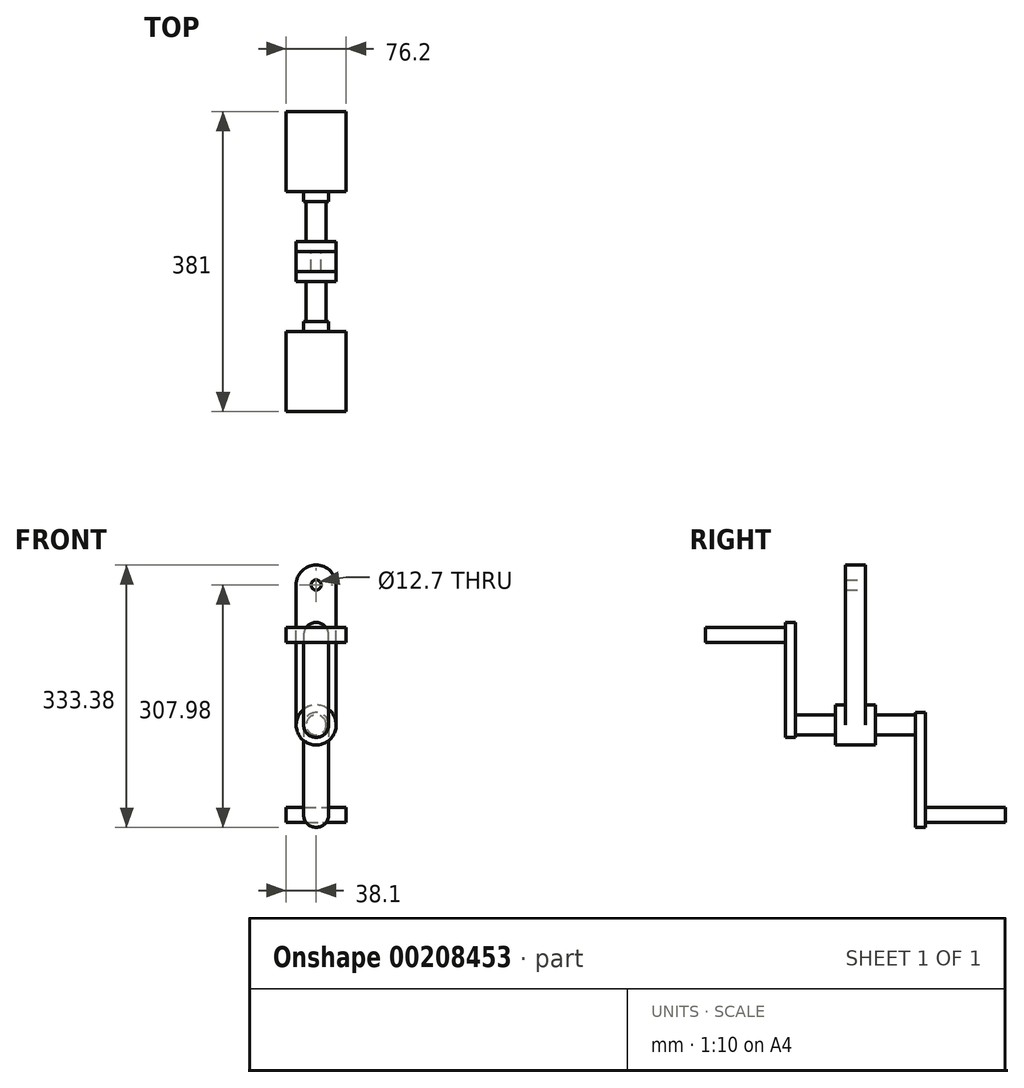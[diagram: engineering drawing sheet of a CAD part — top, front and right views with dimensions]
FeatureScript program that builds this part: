
annotation { "Feature Type Name" : "Feature", "Feature Type Description" : "" }
export const myFeature = defineFeature(function(context is Context, id is Id, definition is map)
    precondition{}
    {
        {
            var Q0;
            Q0=qCreatedBy(makeId("Front.planeOp"),FACE);
            var sketch = newSketch(context, id + "F0", { "sketchPlane" : qUnion([Q0])});
            skCircle(sketch, "E0", {"center": v(0, 0) * mm, "radius": 25.4 * mm});
            skCircle(sketch, "E1", {"center": v(0, 0) * mm, "radius": 12.7 * mm});
            skSolve(sketch);
        }
        {
            var Q0;
            Q0=qSketchRegion(id+"F0",true);
            extrude(context, id + "F1", {"entities" : qUnion([Q0]), "endBound" : BoundingType.SYMMETRIC, "depth" : 50.8 * mm});
        }
        {
            var Q0;
            Q0=qCreatedBy(makeId("Front.planeOp"),FACE);
            var sketch = newSketch(context, id + "F2", { "sketchPlane" : qUnion([Q0])});
            skCircle(sketch, "E2", {"center": v(0, 0) * mm, "radius": 12.7 * mm});
            skSolve(sketch);
        }
        {
            var Q0;
            Q0=qSketchRegion(id+"F2",true);
            extrude(context, id + "F3", {"entities" : qUnion([Q0]), "endBound" : BoundingType.SYMMETRIC, "depth" : 152.4 * mm});
        }
        {
            var Q0;
            Q0=makeQuery(id+"F3.opExtrude","CAP_FACE",FACE,{"disambiguationData":[OSD([sQuery(id+"F2.wireOp",EDGE,"E2")])],"isStart":false});
            var sketch = newSketch(context, id + "F4", { "sketchPlane" : qUnion([Q0])});
            skArc(sketch, "E3", {"start": v(-15.88, 0) * mm, "mid": v(0, -15.88) * mm, "end": v(15.88, 0) * mm});
            skArc(sketch, "E4", {"start": v(15.87, 114.3) * mm, "mid": v(0, 130.18) * mm, "end": v(-15.88, 114.3) * mm});
            skLineSegment(sketch, "E5", {"start": v(-15.88, 114.3) * mm, "end": v(-15.88, 0) * mm});
            skLineSegment(sketch, "E6", {"start": v(15.88, 0) * mm, "end": v(15.88, 114.3) * mm});
            skSolve(sketch);
        }
        {
            var Q0;
            Q0=qSketchRegion(id+"F4",true);
            extrude(context, id + "F5", {"entities" : qUnion([Q0]), "operationType" : NewBodyOperationType.ADD, "depth" : 12.7 * mm});
        }
        {
            var Q0;
            Q0=makeQuery(id+"F5.opExtrude","CAP_FACE",FACE,{"disambiguationData":[OSD([sQuery(id+"F4.wireOp",EDGE,"E3"),sQuery(id+"F4.wireOp",EDGE,"E4"),sQuery(id+"F4.wireOp",EDGE,"E5"),sQuery(id+"F4.wireOp",EDGE,"E6")])],"isStart":false});
            var sketch = newSketch(context, id + "F6", { "sketchPlane" : qUnion([Q0])});
            skLineSegment(sketch, "E7.bottom", {"start": v(38.1, 123.83) * mm, "end": v(-38.1, 123.83) * mm});
            skLineSegment(sketch, "E7.top", {"start": v(38.1, 104.78) * mm, "end": v(-38.1, 104.78) * mm});
            skLineSegment(sketch, "E7.left", {"start": v(38.1, 123.83) * mm, "end": v(38.1, 104.78) * mm});
            skLineSegment(sketch, "E7.right", {"start": v(-38.1, 123.83) * mm, "end": v(-38.1, 104.78) * mm});
            skPoint(sketch, "E7.middle", {"position": v(0, 114.3) * mm});
            skPoint(sketch, "E8.orphan", {"position": v(-15.88, 114.3) * mm});
            skPoint(sketch, "E9.end.orphan", {"position": v(15.88, 114.3) * mm});
            skSolve(sketch);
        }
        {
            var Q0;
            Q0=qSketchRegion(id+"F6",true);
            extrude(context, id + "F7", {"entities" : qUnion([Q0]), "operationType" : NewBodyOperationType.ADD, "depth" : 101.6 * mm});
        }
        {
            var Q0;
            Q0=makeQuery(id+"F3.opExtrude","CAP_FACE",FACE,{"disambiguationData":[OSD([sQuery(id+"F2.wireOp",EDGE,"E2")])],"isStart":true});
            var sketch = newSketch(context, id + "F8", { "sketchPlane" : qUnion([Q0])});
            skArc(sketch, "E10", {"start": v(15.88, 0) * mm, "mid": v(0, 15.88) * mm, "end": v(-15.88, 0) * mm});
            skArc(sketch, "E11", {"start": v(-15.87, -114.3) * mm, "mid": v(0, -130.18) * mm, "end": v(15.88, -114.3) * mm});
            skLineSegment(sketch, "E12", {"start": v(-15.88, 0) * mm, "end": v(-15.88, -114.3) * mm});
            skLineSegment(sketch, "E13", {"start": v(15.88, 0) * mm, "end": v(15.88, -114.3) * mm});
            skSolve(sketch);
        }
        {
            var Q0;
            Q0=qSketchRegion(id+"F8",true);
            extrude(context, id + "F9", {"entities" : qUnion([Q0]), "operationType" : NewBodyOperationType.ADD, "depth" : 12.7 * mm});
        }
        {
            var Q0;
            Q0=makeQuery(id+"F9.opExtrude","CAP_FACE",FACE,{"disambiguationData":[OSD([sQuery(id+"F8.wireOp",EDGE,"E10"),sQuery(id+"F8.wireOp",EDGE,"E11"),sQuery(id+"F8.wireOp",EDGE,"E12"),sQuery(id+"F8.wireOp",EDGE,"E13")])],"isStart":false});
            var sketch = newSketch(context, id + "F10", { "sketchPlane" : qUnion([Q0])});
            skLineSegment(sketch, "E14.bottom", {"start": v(38.1, -104.78) * mm, "end": v(-38.1, -104.78) * mm});
            skLineSegment(sketch, "E14.top", {"start": v(38.1, -123.83) * mm, "end": v(-38.1, -123.83) * mm});
            skLineSegment(sketch, "E14.left", {"start": v(38.1, -104.78) * mm, "end": v(38.1, -123.83) * mm});
            skLineSegment(sketch, "E14.right", {"start": v(-38.1, -104.78) * mm, "end": v(-38.1, -123.83) * mm});
            skPoint(sketch, "E14.middle", {"position": v(0, -114.3) * mm});
            skPoint(sketch, "E15.orphan", {"position": v(-15.88, -114.3) * mm});
            skPoint(sketch, "E16.start.orphan", {"position": v(15.88, -114.3) * mm});
            skSolve(sketch);
        }
        {
            var Q0;
            Q0=qSketchRegion(id+"F10",true);
            extrude(context, id + "F11", {"entities" : qUnion([Q0]), "operationType" : NewBodyOperationType.ADD, "depth" : 101.6 * mm});
        }
        {
            var Q0;
            Q0=qCreatedBy(makeId("Front.planeOp"),FACE);
            var sketch = newSketch(context, id + "F12", { "sketchPlane" : qUnion([Q0])});
            skLineSegment(sketch, "E17.bottom", {"start": v(-25.4, 0) * mm, "end": v(25.4, 0) * mm});
            skLineSegment(sketch, "E17.top", {"start": v(0, 203.2) * mm, "end": v(0, 203.2) * mm});
            skLineSegment(sketch, "E17.left", {"start": v(-25.4, 0) * mm, "end": v(-25.4, 177.8) * mm});
            skLineSegment(sketch, "E17.right", {"start": v(25.4, 0) * mm, "end": v(25.4, 177.8) * mm});
            skPoint(sketch, "E18.visualSharp", {"position": v(-25.4, 203.2) * mm});
            skArc(sketch, "E18.filletArc", {"start": v(0, 203.2) * mm, "mid": v(-17.96, 195.76) * mm, "end": v(-25.4, 177.8) * mm});
            skPoint(sketch, "E19.visualSharp", {"position": v(25.4, 203.2) * mm});
            skArc(sketch, "E19.filletArc", {"start": v(25.4, 177.8) * mm, "mid": v(17.96, 195.76) * mm, "end": v(0, 203.2) * mm});
            skLineSegment(sketch, "E20", {"start": v(0, 0) * mm, "end": v(25.4, 0) * mm});
            skCircle(sketch, "E21", {"center": v(0, 177.8) * mm, "radius": 6.35 * mm});
            skSolve(sketch);
        }
        {
            var Q0;
            Q0=qSketchRegion(id+"F12",true);
            extrude(context, id + "F13", {"entities" : qUnion([Q0]), "operationType" : NewBodyOperationType.ADD, "endBound" : BoundingType.SYMMETRIC, "depth" : 25.4 * mm});
        }
    });
